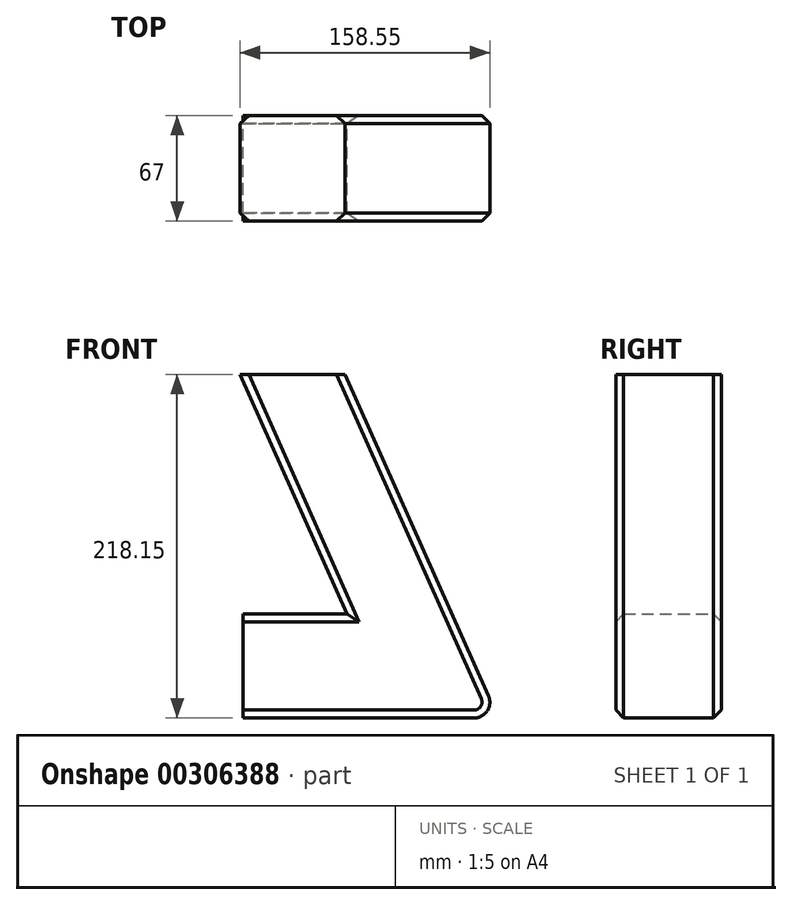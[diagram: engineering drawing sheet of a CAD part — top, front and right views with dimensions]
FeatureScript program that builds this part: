
annotation { "Feature Type Name" : "Feature", "Feature Type Description" : "" }
export const myFeature = defineFeature(function(context is Context, id is Id, definition is map)
    precondition{}
    {
        {
            var Q0;
            Q0=qCreatedBy(makeId("Front.planeOp"),FACE);
            var sketch = newSketch(context, id + "F0", { "sketchPlane" : qUnion([Q0])});
            skLineSegment(sketch, "E0", {"start": v(0, 66) * mm, "end": v(0, 0) * mm});
            skLineSegment(sketch, "E1", {"start": v(0, 0) * mm, "end": v(162.1, 0) * mm});
            skLineSegment(sketch, "E2", {"start": v(162.1, 0) * mm, "end": v(64.8, 218.15) * mm});
            skLineSegment(sketch, "E3", {"start": v(64.8, 218.15) * mm, "end": v(-1.86, 218.15) * mm});
            skLineSegment(sketch, "E4", {"start": v(-1.86, 218.15) * mm, "end": v(66, 66) * mm});
            skLineSegment(sketch, "E5", {"start": v(66, 66) * mm, "end": v(0, 66) * mm});
            skSolve(sketch);
        }
        {
            var Q0;
            Q0=makeQuery(id+"F0.imprint","IMPRINT",FACE,{"disambiguationData":[TD([[makeQuery(id+"F0.imprint","IMPRINT",EDGE,{"derivedFrom":sQuery(id+"F0.wireOp",EDGE,"E0")}),1.0]])]});
            extrude(context, id + "F1", {"entities" : qUnion([Q0]), "depth" : 67 * mm});
        }
        {
            var Q0;
            Q0=makeQuery(id+"F1.opExtrude","SWEPT_EDGE",EDGE,{"disambiguationData":[OSD([sQuery(id+"F0.wireOp",EDGE,"E1"),sQuery(id+"F0.wireOp",EDGE,"E2")])]});
            fillet(context, id + "F2", {"entities" : qUnion([Q0]), "radius" : 10 * mm, "tangentPropagation" : true, "allowEdgeOverflow" : false});
        }
        {
            var Q0;
            Q0=makeQuery(id+"F1.opExtrude","CAP_EDGE",EDGE,{"disambiguationData":[OSD([sQuery(id+"F0.wireOp",EDGE,"E2")])],"isStart":false});
            var Q1;
            Q1=makeQuery(id+"F1.opExtrude","CAP_EDGE",EDGE,{"disambiguationData":[OSD([sQuery(id+"F0.wireOp",EDGE,"E2")])],"isStart":true});
            var Q2;
            Q2=makeQuery(id+"F1.opExtrude","CAP_EDGE",EDGE,{"disambiguationData":[OSD([sQuery(id+"F0.wireOp",EDGE,"E4")])],"isStart":false});
            var Q3;
            Q3=makeQuery(id+"F1.opExtrude","CAP_EDGE",EDGE,{"disambiguationData":[OSD([sQuery(id+"F0.wireOp",EDGE,"E4")])],"isStart":true});
            var Q4;
            Q4=makeQuery(id+"F1.opExtrude","CAP_EDGE",EDGE,{"disambiguationData":[OSD([sQuery(id+"F0.wireOp",EDGE,"E5")])],"isStart":true});
            var Q5;
            Q5=makeQuery(id+"F1.opExtrude","CAP_EDGE",EDGE,{"disambiguationData":[OSD([sQuery(id+"F0.wireOp",EDGE,"E5")])],"isStart":false});
            chamfer(context, id + "F3", {"entities" : qUnion([Q0, Q1, Q2, Q3, Q4, Q5]), "width" : 5 * mm, "tangentPropagation" : true});
        }
    });
